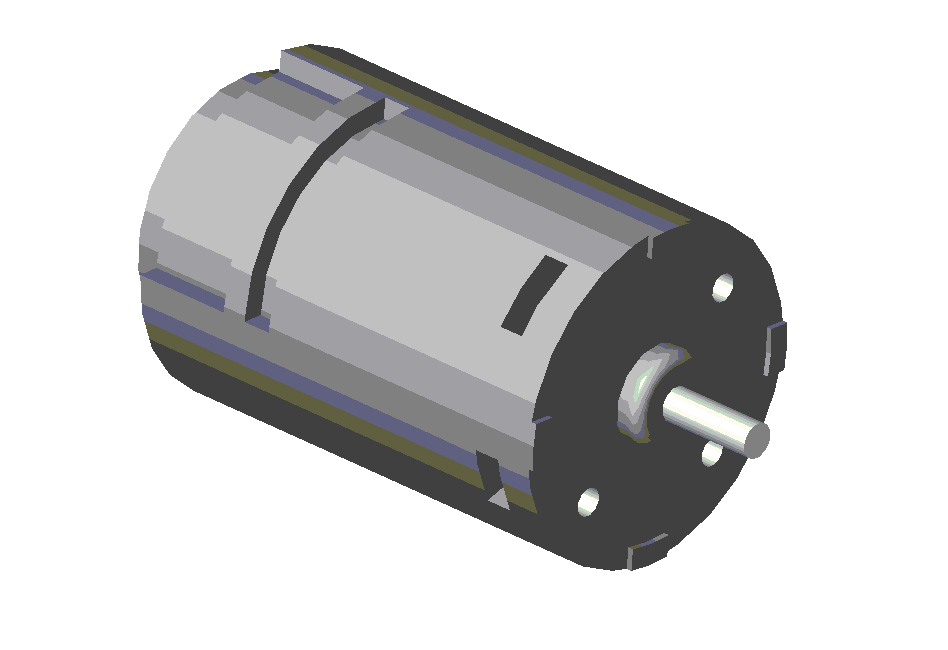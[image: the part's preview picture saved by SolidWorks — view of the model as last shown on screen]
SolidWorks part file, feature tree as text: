
SOLIDWORKS PART (.sldprt)
format: sldprt  version: not decoded by parser v0  size: 315,392 bytes
history: native  units: mm
features: sketch x9, cut_extrude x5, extrude x4, plane x4, pattern_circular x4, fillet x1 (+8 scaffold rows collapsed)
feature tree (35):
  scaffold x8  (default folders/planes/origin — collapsed)
  sketch  "Sketch1"  dims[D1=47.5mm]
  extrude  "Base-Extrude"  Depth=73.12mm
  plane  "Plane1"  Offset=7.78mm
  sketch  "Sketch3"  dims[D1=14.6mm]
  extrude  "Boss-Extrude2"  Depth=3.5mm
  sketch  "Sketch4"  dims[D1=5.0mm]
  extrude  "Boss-Extrude3"  Depth=14.25mm
  sketch  "Sketch5"  dims[D1=4.0mm D2=16.4mm]
  cut_extrude  "Cut-Extrude2"  Depth=8mm
  pattern_circular  "CirPattern1"  Count=3 Angle=90deg
  fillet  "Fillet1"  Radius=2mm
  sketch  "Sketch7"  dims[c1.D4=47.5mm c1.D5=41.5mm c1.D1=~31.582668mm c2.D1=45.0deg c2.D2=6.7mm c2.D3=3.35mm c3.D1=~12.111178mm c3.D3=~16.848794mm c3.D6=~3.034757mm]
  extrude  "Boss-Extrude4"  Depth=0.8mm
  pattern_circular  "CirPattern2"  Count=4 Angle=90deg
  plane  "Plane2"  Offset=5.33mm
  sketch  "Sketch8"  dims[c1.D5=~18.930773mm c1.D6=23.75mm c2.D5=~18.930773mm c2.D6=23.75mm c2.D1=4.0mm c2.D2=8.0mm c3.D1=4.0mm c3.D3=5.5mm c3.D4=11.0mm c4.D1=~4.990185mm c5.D1=65.0deg c5.D2=4.25mm c5.D7=8.5mm c6.D1=~4.990185mm c7.D1=65.0deg c7.D2=~4.919105mm]
  cut_extrude  "Cut-Extrude4"  Depth=3.9mm
  pattern_circular  "CirPattern3"  Count=2 Angle=180deg
  sketch  "Sketch9"  dims[D1=37.0mm]
  cut_extrude  "Cut-Extrude5"  Depth=5.3mm
  plane  "Plane3"  Offset=45.4mm
  sketch  "Sketch10"  dims[D1=15.0mm D2=30.0mm]
  cut_extrude  "Cut-Extrude6"  Depth=4.2mm
  plane  "Plane4"  Offset=3.65mm
  sketch  "Sketch12"  dims[D1=3.0mm]
  cut_extrude  "Cut-Extrude9"  [1 undecoded]
  pattern_circular  "CirPattern4"  Count=2 Angle=180deg
decode coverage: 22 of 23 modeling features carry decoded parameters
note: ~ marks probable driven/reference dimensions
note: 1 parameter value undecoded
note: suppression state not decoded; provenance and decode notes live in map.json
